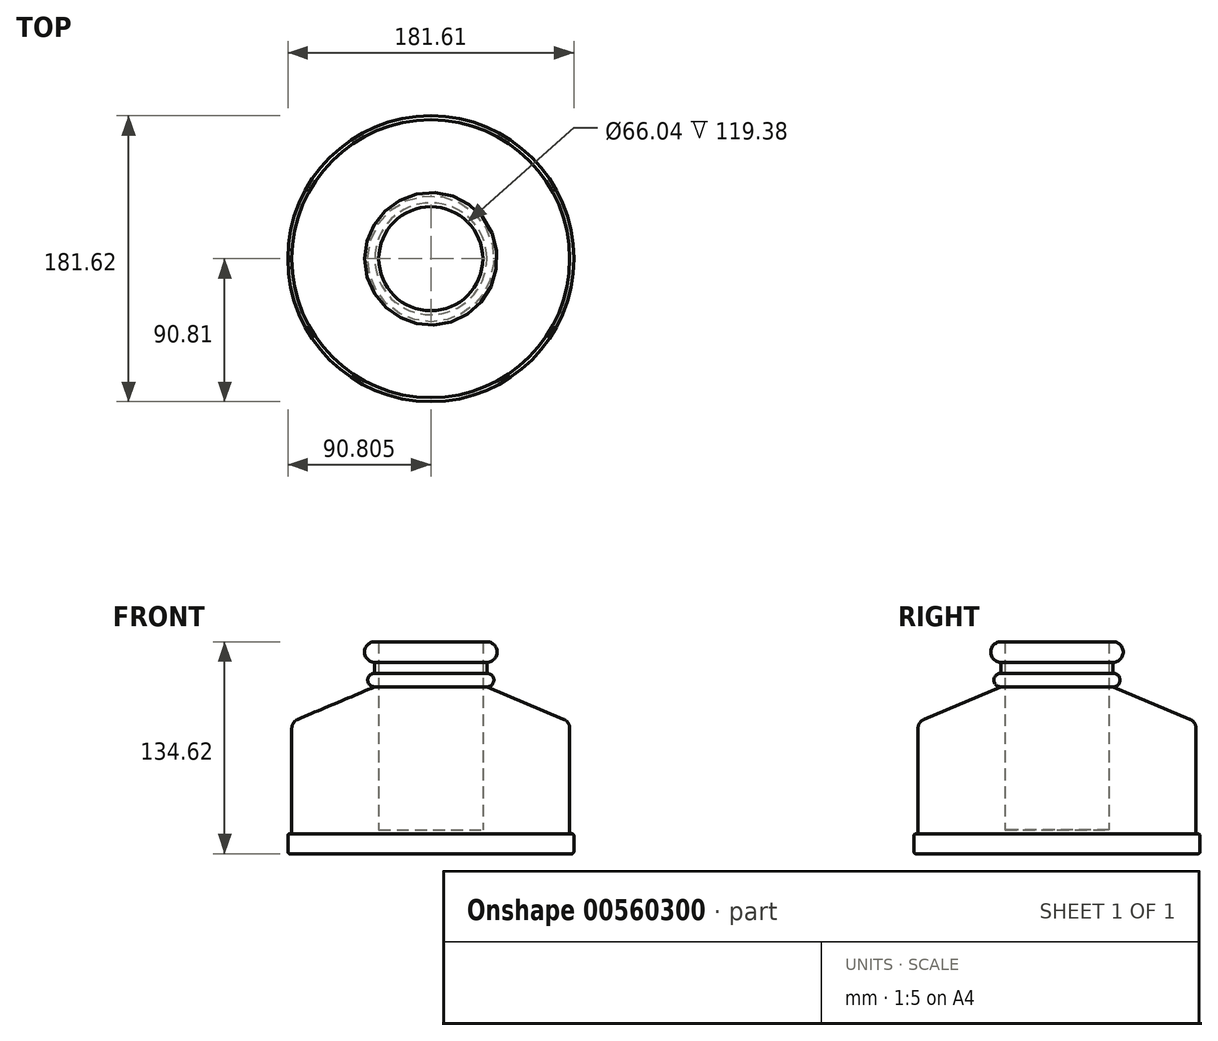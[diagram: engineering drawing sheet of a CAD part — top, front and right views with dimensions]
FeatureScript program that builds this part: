
annotation { "Feature Type Name" : "Feature", "Feature Type Description" : "" }
export const myFeature = defineFeature(function(context is Context, id is Id, definition is map)
    precondition{}
    {
        {
            var Q0;
            Q0=qCreatedBy(makeId("Front.planeOp"),FACE);
            var sketch = newSketch(context, id + "F0", { "sketchPlane" : qUnion([Q0])});
            skLineSegment(sketch, "E0.left", {"start": v(0, 1.27) * mm, "end": v(0, 66.9) * mm});
            skLineSegment(sketch, "E1", {"start": v(55.24, 121.92) * mm, "end": v(55.25, 2.54) * mm});
            skLineSegment(sketch, "E2", {"start": v(52.7, 121.92) * mm, "end": v(55.24, 121.92) * mm});
            skArc(sketch, "E3", {"start": v(52.7, 121.92) * mm, "mid": v(46.2, 115.4) * mm, "end": v(52.7, 108.9) * mm});
            skLineSegment(sketch, "E4", {"start": v(52.7, 108.9) * mm, "end": v(52.7, 101.94) * mm});
            skArc(sketch, "E5", {"start": v(52.7, 101.94) * mm, "mid": v(48.22, 97.62) * mm, "end": v(52.7, 93.3) * mm});
            skLineSegment(sketch, "E6", {"start": v(-1.27, 0) * mm, "end": v(-1.27, 0) * mm});
            skLineSegment(sketch, "E7", {"start": v(-2.54, -1.27) * mm, "end": v(-2.54, -11.43) * mm});
            skPoint(sketch, "E8.visualSharp", {"position": v(-2.54, -12.7) * mm});
            skArc(sketch, "E8.filletArc", {"start": v(-2.54, -11.43) * mm, "mid": v(-2.17, -12.33) * mm, "end": v(-1.27, -12.7) * mm});
            skPoint(sketch, "E9.visualSharp", {"position": v(-2.54, 0) * mm});
            skArc(sketch, "E9.filletArc", {"start": v(-1.27, 0) * mm, "mid": v(-2.17, -0.37) * mm, "end": v(-2.54, -1.27) * mm});
            skPoint(sketch, "E10.visualSharp", {"position": v(0, 0) * mm});
            skArc(sketch, "E10.filletArc", {"start": v(-1.27, 0) * mm, "mid": v(-0.37, 0.37) * mm, "end": v(0, 1.27) * mm});
            skPoint(sketch, "E11.endSnap0", {"position": v(88.27, 2.54) * mm});
            skLineSegment(sketch, "E12", {"start": v(88.27, 2.54) * mm, "end": v(55.25, 2.54) * mm});
            skLineSegment(sketch, "E13", {"start": v(88.27, -12.7) * mm, "end": v(88.27, 2.54) * mm});
            skLineSegment(sketch, "E14", {"start": v(88.27, -12.7) * mm, "end": v(-1.27, -12.7) * mm});
            skLineSegment(sketch, "E15", {"start": v(88.27, -12.7) * mm, "end": v(88.27, 142.13) * mm, "construction": true});
            skLineSegment(sketch, "E16", {"start": v(3.89, 72.76) * mm, "end": v(52.7, 93.3) * mm});
            skPoint(sketch, "E17.visualSharp", {"position": v(0, 71.12) * mm});
            skArc(sketch, "E18.filletArc", {"start": v(3.89, 72.76) * mm, "mid": v(1.06, 70.42) * mm, "end": v(0, 66.9) * mm});
            skSolve(sketch);
        }
        {
            var Q0;
            Q0=makeQuery(id+"F0.imprint","IMPRINT",FACE,{"disambiguationData":[TD([[makeQuery(id+"F0.imprint","IMPRINT",EDGE,{"derivedFrom":sQuery(id+"F0.wireOp",EDGE,"E0.left")}),-1.0]])]});
            var Q1;
            Q1=sQuery(id+"F0.wireOp",EDGE,"E15");
            revolve(context, id + "F1", {"entities" : qUnion([Q0]), "axis" : qUnion([Q1]), "revolveType" : RevolveType.FULL});
        }
    });
